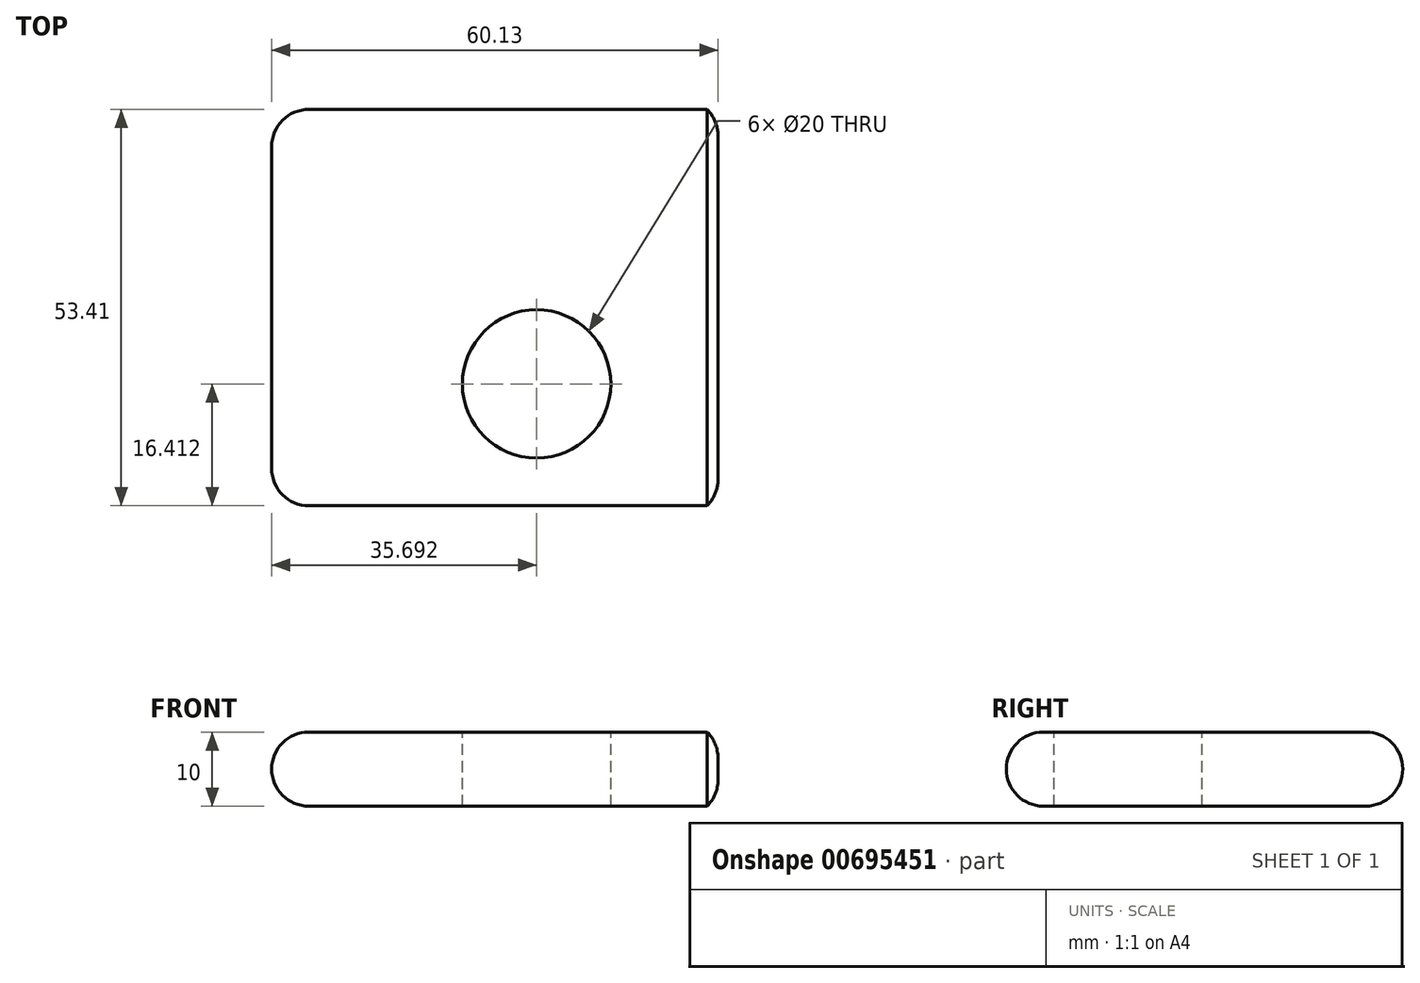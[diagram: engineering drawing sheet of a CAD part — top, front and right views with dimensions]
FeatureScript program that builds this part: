
annotation { "Feature Type Name" : "Feature", "Feature Type Description" : "" }
export const myFeature = defineFeature(function(context is Context, id is Id, definition is map)
    precondition{}
    {
        {
            var Q0;
            Q0=qCreatedBy(makeId("Top.planeOp"),FACE);
            var sketch = newSketch(context, id + "F0", { "sketchPlane" : qUnion([Q0])});
            skLineSegment(sketch, "E0.bottom", {"start": v(-35.59, 37.44) * mm, "end": v(28.08, 37.44) * mm});
            skLineSegment(sketch, "E0.top", {"start": v(-35.59, -15.97) * mm, "end": v(28.08, -15.97) * mm});
            skLineSegment(sketch, "E0.left", {"start": v(-35.59, 37.44) * mm, "end": v(-35.59, -15.97) * mm});
            skLineSegment(sketch, "E0.right", {"start": v(28.08, 37.44) * mm, "end": v(28.08, -15.97) * mm});
            skSolve(sketch);
        }
        {
            var Q0;
            Q0 = qSketchRegion(id + "F0", true);
            extrude(context, id + "F1", {"entities" : qUnion([Q0]), "depth" : 10 * mm, "offsetDistance" : 25.4 * mm});
        }
        {
            var Q0;
            Q0=makeQuery(id+"F1.opExtrude","CAP_FACE",FACE,{"disambiguationData":[OSD([sQuery(id+"F0.wireOp",EDGE,"E0.bottom"),sQuery(id+"F0.wireOp",EDGE,"E0.top"),sQuery(id+"F0.wireOp",EDGE,"E0.left"),sQuery(id+"F0.wireOp",EDGE,"E0.right")])],"isStart":false});
            var sketch = newSketch(context, id + "F2", { "sketchPlane" : qUnion([Q0])});
            skCircle(sketch, "E1", {"center": v(0.1, 0.44) * mm, "radius": 10 * mm});
            skSolve(sketch);
        }
        {
            var Q0;
            Q0 = qSketchRegion(id + "F2", true);
            extrude(context, id + "F3", {"entities" : qUnion([Q0]), "operationType" : NewBodyOperationType.REMOVE, "oppositeDirection" : true, "depth" : 25 * mm, "offsetDistance" : 25 * mm});
        }
        {
            var Q0;
            Q0=makeQuery(id+"F1.opExtrude","CAP_EDGE",EDGE,{"disambiguationData":[OSD([sQuery(id+"F0.wireOp",EDGE,"E0.left")])],"isStart":false});
            var Q1;
            Q1=makeQuery(id+"F1.opExtrude","SWEPT_FACE",FACE,{"disambiguationData":[OSD([sQuery(id+"F0.wireOp",EDGE,"E0.left")])]});
            fillet(context, id + "F4", {"entities" : qUnion([Q0, Q1]), "radius" : 5 * mm, "tangentPropagation" : true, "allowEdgeOverflow" : false});
        }
        {
            var Q0;
            Q0=makeQuery(id+"F4.opFillet","BLEND_FACE",FACE,{"disambiguationData":[OSD([sQuery(id+"F0.wireOp",EDGE,"E0.left")])]});
            fillet(context, id + "F5", {"entities" : qUnion([Q0]), "radius" : 5 * mm, "tangentPropagation" : true, "allowEdgeOverflow" : false});
        }
        {
            var Q0;
            Q0=makeQuery(id+"F1.opExtrude","CAP_EDGE",EDGE,{"disambiguationData":[OSD([sQuery(id+"F0.wireOp",EDGE,"E0.right")])],"isStart":false});
            chamfer(context, id + "F6", {"entities" : qUnion([Q0]), "width" : 5 * mm, "tangentPropagation" : true});
        }
        {
            var Q0;
            {var subQ0=sQuery(id+"F0.wireOp",EDGE,"E0.right");Q0=makeQuery(id+"F6.opChamfer","BLEND_EDGE",EDGE,{"blendedFrom":[makeQuery(id+"F1.opExtrude","CAP_EDGE",EDGE,{"disambiguationData":[OSD([subQ0])],"isStart":true}),makeQuery(id+"F1.opExtrude","CAP_EDGE",EDGE,{"disambiguationData":[OSD([subQ0])],"isStart":false})],"blendedInto":[]});}
            chamfer(context, id + "F7", {"entities" : qUnion([Q0]), "width" : 5 * mm, "tangentPropagation" : true});
        }
        {
            var Q0;
            {var subQ0=sQuery(id+"F0.wireOp",EDGE,"E0.right");var subQ1=makeQuery(id+"F1.opExtrude","CAP_EDGE",EDGE,{"disambiguationData":[OSD([subQ0])],"isStart":false});Q0=makeQuery(id+"F7.opChamfer","BLEND_EDGE",EDGE,{"blendedFrom":[makeQuery(id+"F6.opChamfer","BLEND_EDGE",EDGE,{"blendedFrom":[makeQuery(id+"F1.opExtrude","CAP_EDGE",EDGE,{"disambiguationData":[OSD([subQ0])],"isStart":true}),subQ1],"blendedInto":[]}),makeQuery(id+"F6.opChamfer","BLEND_FACE",FACE,{"disambiguationData":[OSD([subQ0]),TDD([subQ1])]})],"blendedInto":[makeQuery(id+"F6.opChamfer","BLEND_FACE",FACE,{"disambiguationData":[OSD([subQ0]),TDD([subQ1])]})]});}
            var Q1;
            {var subQ0=sQuery(id+"F0.wireOp",EDGE,"E0.right");Q1=makeQuery(id+"F7.opChamfer","BLEND_EDGE",EDGE,{"blendedFrom":[makeQuery(id+"F6.opChamfer","BLEND_EDGE",EDGE,{"blendedFrom":[makeQuery(id+"F1.opExtrude","CAP_EDGE",EDGE,{"disambiguationData":[OSD([subQ0])],"isStart":true}),makeQuery(id+"F1.opExtrude","CAP_EDGE",EDGE,{"disambiguationData":[OSD([subQ0])],"isStart":false})],"blendedInto":[]}),makeQuery(id+"F6.opChamfer","BLEND_FACE",FACE,{"disambiguationData":[OSD([sQuery(id+"F0.wireOp",EDGE,"E0.bottom"),subQ0])]})],"blendedInto":[makeQuery(id+"F6.opChamfer","BLEND_FACE",FACE,{"disambiguationData":[OSD([sQuery(id+"F0.wireOp",EDGE,"E0.bottom"),subQ0])]})]});}
            fillet(context, id + "F8", {"entities" : qUnion([Q0, Q1]), "radius" : 5 * mm, "tangentPropagation" : true, "allowEdgeOverflow" : false});
        }
    });
